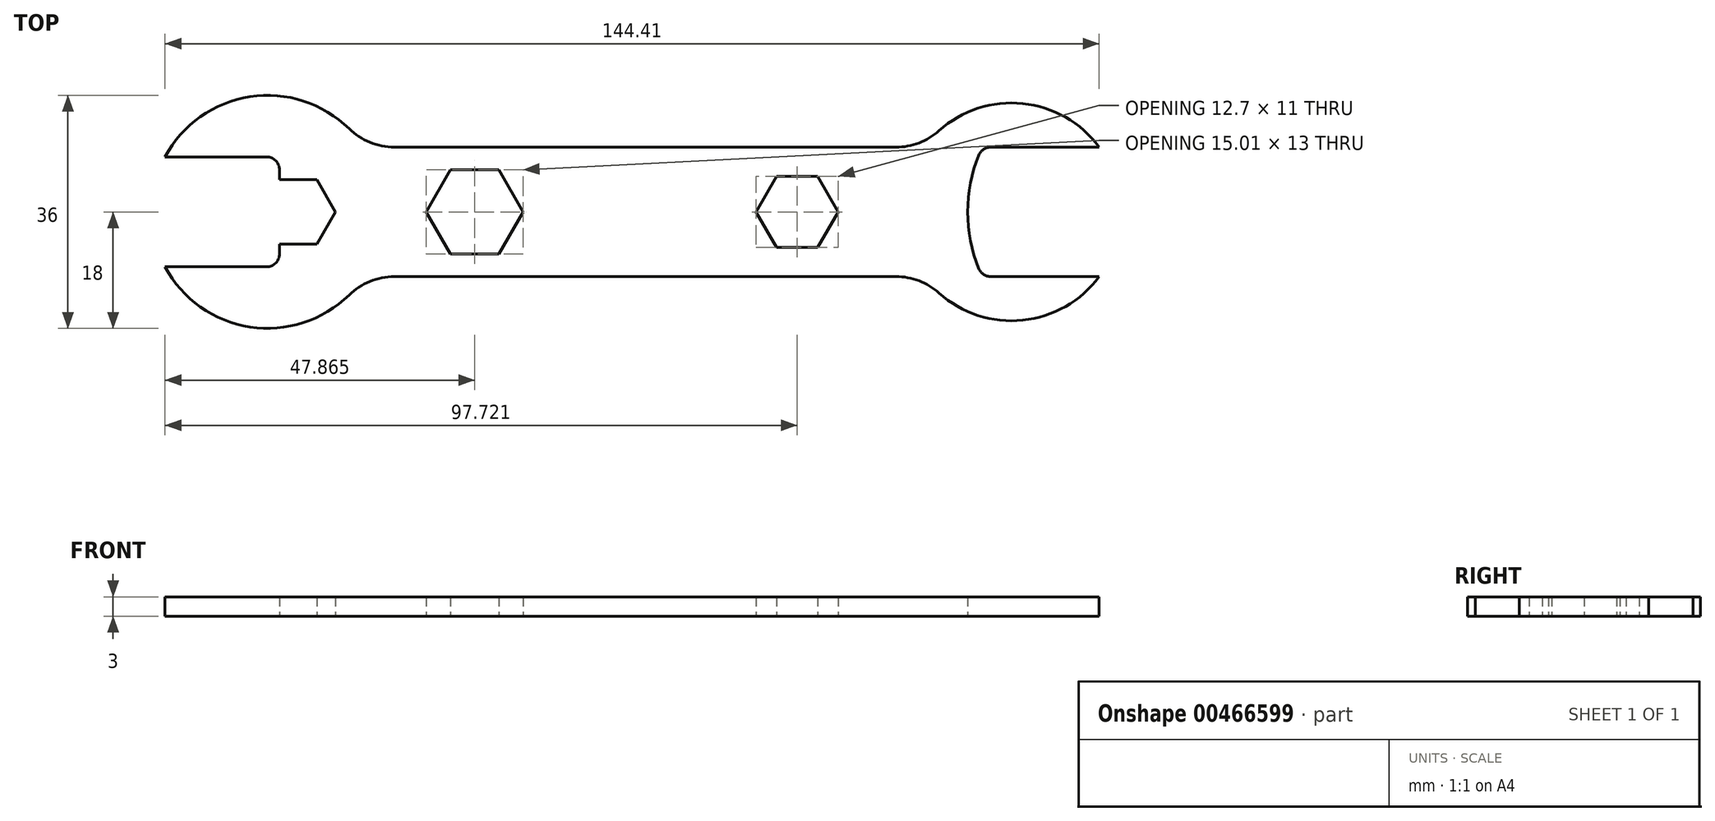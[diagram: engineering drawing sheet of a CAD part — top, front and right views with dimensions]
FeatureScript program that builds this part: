
annotation { "Feature Type Name" : "Feature", "Feature Type Description" : "" }
export const myFeature = defineFeature(function(context is Context, id is Id, definition is map)
    precondition{}
    {
        {
            var Q0;
            Q0=qCreatedBy(makeId("Top.planeOp"),FACE);
            var sketch = newSketch(context, id + "F0", { "sketchPlane" : qUnion([Q0])});
            skArc(sketch, "E0", {"start": v(-44.9, 12.86) * mm, "mid": v(-60.22, 17.8) * mm, "end": v(-73.37, 8.5) * mm});
            skArc(sketch, "E1", {"start": v(46.28, -12.55) * mm, "mid": v(59.22, -16.74) * mm, "end": v(71.04, -10) * mm});
            skLineSegment(sketch, "E2.bottom", {"start": v(39.61, 10) * mm, "end": v(-37.9, 10) * mm});
            skLineSegment(sketch, "E2.top", {"start": v(39.61, -10) * mm, "end": v(-37.9, -10) * mm});
            skPoint(sketch, "E2.middle", {"position": v(0, 0) * mm});
            skPoint(sketch, "E2.right.start.orphan", {"position": v(-51.3, 10) * mm});
            skPoint(sketch, "E3.orphan", {"position": v(-51.3, -10) * mm});
            skPoint(sketch, "E2.left.start.orphan", {"position": v(51.3, 10) * mm});
            skPoint(sketch, "E4.orphan", {"position": v(51.3, -10) * mm});
            skPoint(sketch, "E5.visualSharp", {"position": v(43.96, 10) * mm});
            skArc(sketch, "E5.filletArc", {"start": v(39.61, 10) * mm, "mid": v(43.18, 10.66) * mm, "end": v(46.28, 12.55) * mm});
            skPoint(sketch, "E6.visualSharp", {"position": v(43.96, -10) * mm});
            skArc(sketch, "E6.filletArc", {"start": v(46.28, -12.55) * mm, "mid": v(43.18, -10.66) * mm, "end": v(39.61, -10) * mm});
            skPoint(sketch, "E7.visualSharp", {"position": v(-42.53, -10) * mm});
            skArc(sketch, "E7.filletArc", {"start": v(-37.9, -10) * mm, "mid": v(-41.68, -10.74) * mm, "end": v(-44.9, -12.86) * mm});
            skPoint(sketch, "E8.visualSharp", {"position": v(-42.53, 10) * mm});
            skArc(sketch, "E8.filletArc", {"start": v(-44.9, 12.86) * mm, "mid": v(-41.68, 10.74) * mm, "end": v(-37.9, 10) * mm});
            skCircle(sketch, "E9.cCircle", {"center": v(-25.5, 0) * mm, "radius": 6.5 * mm, "construction": true});
            skLineSegment(sketch, "E9.0", {"start": v(-29.26, 6.5) * mm, "end": v(-21.75, 6.5) * mm});
            skLineSegment(sketch, "E9.1", {"start": v(-21.75, 6.5) * mm, "end": v(-18, 0) * mm});
            skLineSegment(sketch, "E9.2", {"start": v(-18, 0) * mm, "end": v(-21.75, -6.5) * mm});
            skLineSegment(sketch, "E9.3", {"start": v(-21.75, -6.5) * mm, "end": v(-29.26, -6.5) * mm});
            skLineSegment(sketch, "E9.4", {"start": v(-29.26, -6.5) * mm, "end": v(-33.01, 0) * mm});
            skLineSegment(sketch, "E9.5", {"start": v(-33.01, 0) * mm, "end": v(-29.26, 6.5) * mm});
            skPoint(sketch, "E9.0.midPoint", {"position": v(-25.5, 6.5) * mm});
            skCircle(sketch, "E10.cCircle", {"center": v(24.35, 0) * mm, "radius": 5.5 * mm, "construction": true});
            skLineSegment(sketch, "E10.0", {"start": v(21.18, 5.5) * mm, "end": v(27.53, 5.5) * mm});
            skLineSegment(sketch, "E10.1", {"start": v(27.53, 5.5) * mm, "end": v(30.7, 0) * mm});
            skLineSegment(sketch, "E10.2", {"start": v(30.7, 0) * mm, "end": v(27.53, -5.5) * mm});
            skLineSegment(sketch, "E10.3", {"start": v(27.53, -5.5) * mm, "end": v(21.18, -5.5) * mm});
            skLineSegment(sketch, "E10.4", {"start": v(21.18, -5.5) * mm, "end": v(18, 0) * mm});
            skLineSegment(sketch, "E10.5", {"start": v(18, 0) * mm, "end": v(21.18, 5.5) * mm});
            skPoint(sketch, "E10.0.midPoint", {"position": v(24.35, 5.5) * mm});
            skLineSegment(sketch, "E11.bottom", {"start": v(71.04, 10) * mm, "end": v(54.29, 10) * mm});
            skLineSegment(sketch, "E11.top", {"start": v(71.04, -10) * mm, "end": v(54.29, -10) * mm});
            skPoint(sketch, "E11.middle", {"position": v(70.19, 0) * mm});
            skArc(sketch, "E12", {"start": v(52.44, 8.76) * mm, "mid": v(50.7, 0) * mm, "end": v(52.44, -8.76) * mm});
            skPoint(sketch, "E11.left.start.orphan", {"position": v(87.39, 10) * mm});
            skArc(sketch, "E13.trimOffspring", {"start": v(71.04, 10) * mm, "mid": v(59.22, 16.74) * mm, "end": v(46.28, 12.55) * mm});
            skPoint(sketch, "E14.orphan", {"position": v(87.39, -10) * mm});
            skArc(sketch, "E15.cCircle", {"start": v(-52.78, -5) * mm, "mid": v(-47.78, 0) * mm, "end": v(-52.78, 5) * mm, "construction": true});
            skLineSegment(sketch, "E15.0", {"start": v(-52.78, 5) * mm, "end": v(-49.9, 5) * mm});
            skLineSegment(sketch, "E15.1", {"start": v(-49.9, 5) * mm, "end": v(-47.01, 0) * mm});
            skLineSegment(sketch, "E15.2", {"start": v(-47.01, 0) * mm, "end": v(-49.9, -5) * mm});
            skLineSegment(sketch, "E15.3", {"start": v(-49.9, -5) * mm, "end": v(-52.78, -5) * mm});
            skPoint(sketch, "E15.0.midPoint", {"position": v(-52.78, 5) * mm});
            skLineSegment(sketch, "E16.bottom", {"start": v(-57.67, 8.5) * mm, "end": v(-73.37, 8.5) * mm});
            skLineSegment(sketch, "E16.top", {"start": v(-57.67, -8.5) * mm, "end": v(-73.37, -8.5) * mm});
            skPoint(sketch, "E16.middle", {"position": v(-70.62, 0) * mm});
            skArc(sketch, "E17.trimOffspring", {"start": v(-73.37, -8.5) * mm, "mid": v(-60.22, -17.8) * mm, "end": v(-44.9, -12.86) * mm});
            skPoint(sketch, "E16.right.start.orphan", {"position": v(-88.45, 8.5) * mm});
            skPoint(sketch, "E18.orphan", {"position": v(-88.45, -8.5) * mm});
            skPoint(sketch, "E19.orphan", {"position": v(-55.67, 5) * mm});
            skPoint(sketch, "E20.visualSharp", {"position": v(-52.78, 8.5) * mm});
            skPoint(sketch, "E21.visualSharp", {"position": v(-52.78, -8.5) * mm});
            skPoint(sketch, "E22.visualSharp", {"position": v(52.99, 10) * mm});
            skArc(sketch, "E22.filletArc", {"start": v(54.29, 10) * mm, "mid": v(53.17, 9.66) * mm, "end": v(52.44, 8.76) * mm});
            skPoint(sketch, "E23.visualSharp", {"position": v(52.99, -10) * mm});
            skArc(sketch, "E23.filletArc", {"start": v(52.44, -8.76) * mm, "mid": v(53.17, -9.66) * mm, "end": v(54.29, -10) * mm});
            skLineSegment(sketch, "E24", {"start": v(-52.78, 5) * mm, "end": v(-52.78, 0) * mm, "construction": true});
            skLineSegment(sketch, "E25.MirrorCS", {"start": v(-52.78, 5) * mm, "end": v(-55.67, 5) * mm});
            skLineSegment(sketch, "E26.MirrorCS", {"start": v(-55.67, -5) * mm, "end": v(-52.78, -5) * mm});
            skLineSegment(sketch, "E27", {"start": v(-55.67, 5) * mm, "end": v(-55.67, 6.5) * mm});
            skLineSegment(sketch, "E28", {"start": v(-55.67, -5) * mm, "end": v(-55.67, -6.5) * mm});
            skPoint(sketch, "E29.MirrorCS.start.orphan", {"position": v(-58.56, 0) * mm});
            skPoint(sketch, "E30.visualSharp", {"position": v(-55.67, 8.5) * mm});
            skArc(sketch, "E30.filletArc", {"start": v(-55.67, 6.5) * mm, "mid": v(-56.26, 7.91) * mm, "end": v(-57.67, 8.5) * mm});
            skPoint(sketch, "E31.visualSharp", {"position": v(-55.67, -8.5) * mm});
            skArc(sketch, "E31.filletArc", {"start": v(-57.67, -8.5) * mm, "mid": v(-56.26, -7.91) * mm, "end": v(-55.67, -6.5) * mm});
            skSolve(sketch);
        }
        {
            var Q0;
            Q0=makeQuery(id+"F0.imprint","IMPRINT",FACE,{"disambiguationData":[TD([[makeQuery(id+"F0.imprint","IMPRINT",EDGE,{"derivedFrom":sQuery(id+"F0.wireOp",EDGE,"E0")}),1.0]])]});
            extrude(context, id + "F1", {"entities" : qUnion([Q0]), "depth" : 3 * mm});
        }
    });
